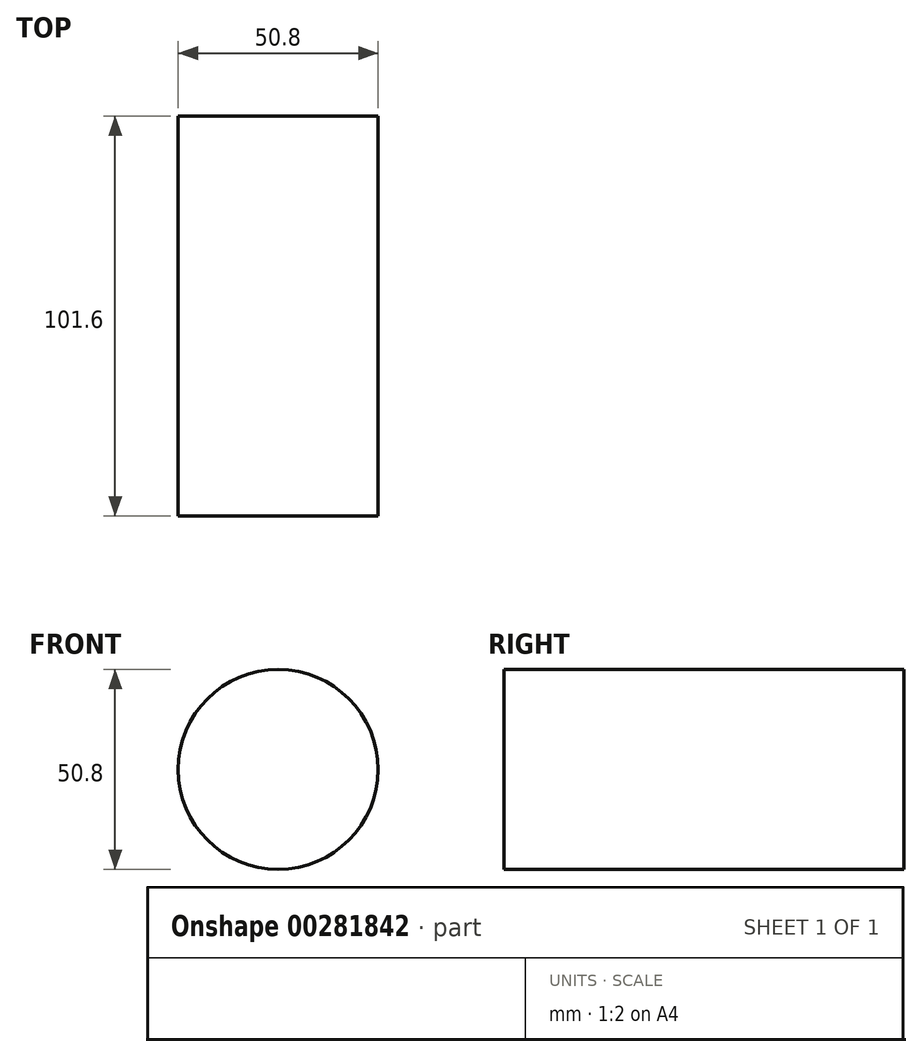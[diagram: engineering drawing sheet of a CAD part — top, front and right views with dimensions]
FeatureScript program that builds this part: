
annotation { "Feature Type Name" : "Feature", "Feature Type Description" : "" }
export const myFeature = defineFeature(function(context is Context, id is Id, definition is map)
    precondition{}
    {
        {
            var Q0;
            Q0=qCreatedBy(makeId("Front.planeOp"),FACE);
            var sketch = newSketch(context, id + "F0", { "sketchPlane" : qUnion([Q0])});
            skCircle(sketch, "E0", {"center": v(1.34, 0) * mm, "radius": 25.4 * mm});
            skSolve(sketch);
        }
        {
            var Q0;
            Q0 = qSketchRegion(id + "F0", true);
            extrude(context, id + "F1", {"entities" : qUnion([Q0]), "depth" : 101.6 * mm});
        }
    });
